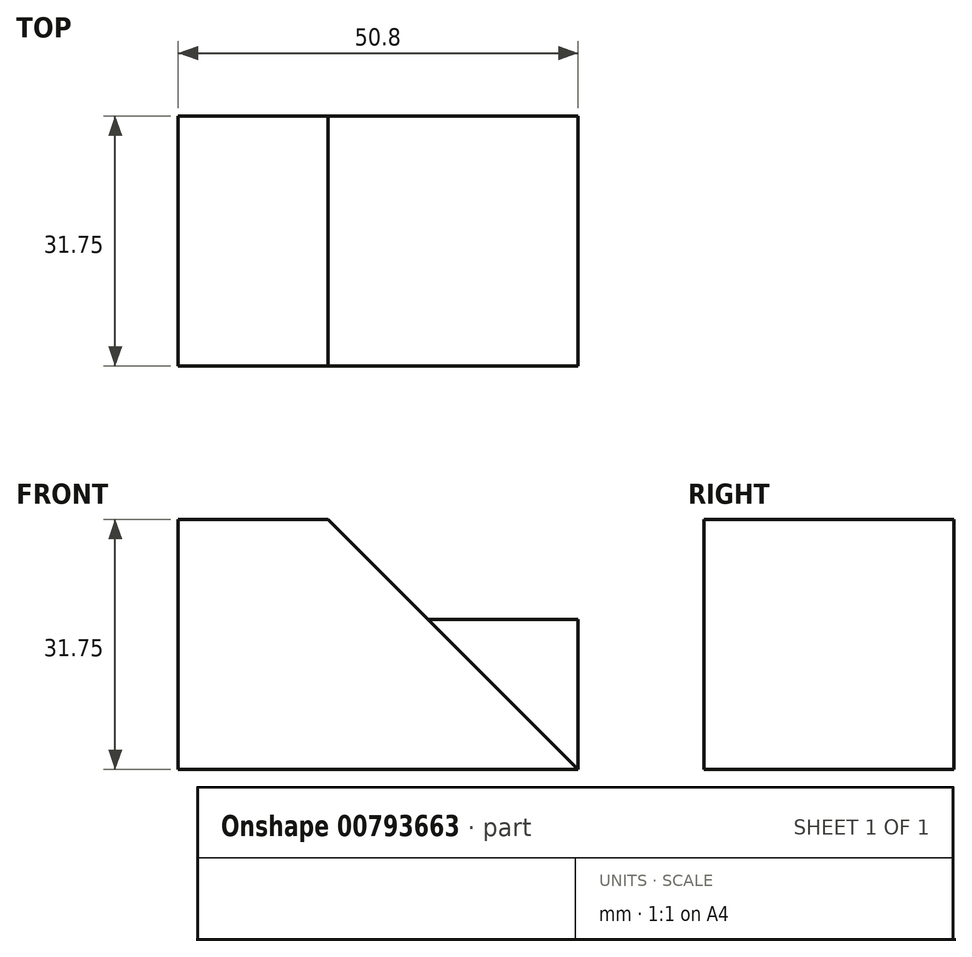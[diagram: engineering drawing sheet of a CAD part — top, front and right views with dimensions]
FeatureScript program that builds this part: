
annotation { "Feature Type Name" : "Feature", "Feature Type Description" : "" }
export const myFeature = defineFeature(function(context is Context, id is Id, definition is map)
    precondition{}
    {
        {
            var Q0;
            Q0=qCreatedBy(makeId("Front.planeOp"),FACE);
            var sketch = newSketch(context, id + "F0", { "sketchPlane" : qUnion([Q0])});
            skLineSegment(sketch, "E0", {"start": v(0, 0) * mm, "end": v(0, 31.75) * mm});
            skLineSegment(sketch, "E1", {"start": v(0, 31.75) * mm, "end": v(19.05, 31.75) * mm});
            skLineSegment(sketch, "E2", {"start": v(19.05, 31.75) * mm, "end": v(50.8, 0) * mm});
            skLineSegment(sketch, "E3", {"start": v(50.8, 0) * mm, "end": v(0, 0) * mm});
            skSolve(sketch);
        }
        {
            var Q0;
            Q0=makeQuery(id+"F0.imprint","IMPRINT",FACE,{"disambiguationData":[TD([[makeQuery(id+"F0.imprint","IMPRINT",EDGE,{"derivedFrom":sQuery(id+"F0.wireOp",EDGE,"E0")}),-1.0]])]});
            extrude(context, id + "F1", {"entities" : qUnion([Q0]), "depth" : 31.75 * mm, "offsetDistance" : 25.4 * mm});
        }
        {
            var Q0;
            Q0=qCreatedBy(makeId("Front.planeOp"),FACE);
            var sketch = newSketch(context, id + "F2", { "sketchPlane" : qUnion([Q0])});
            skLineSegment(sketch, "E4", {"start": v(50.8, 0) * mm, "end": v(50.8, 19.05) * mm});
            skLineSegment(sketch, "E5", {"start": v(50.8, 19.05) * mm, "end": v(31.75, 19.05) * mm});
            skLineSegment(sketch, "E6", {"start": v(31.75, 19.05) * mm, "end": v(50.8, 0) * mm});
            skSolve(sketch);
        }
        {
            var Q0;
            Q0=qSketchRegion(id+"F2",true);
            extrude(context, id + "F3", {"entities" : qUnion([Q0]), "operationType" : NewBodyOperationType.ADD, "depth" : 3 / 101.6 * mm, "offsetDistance" : 25.4 * mm});
        }
    });
